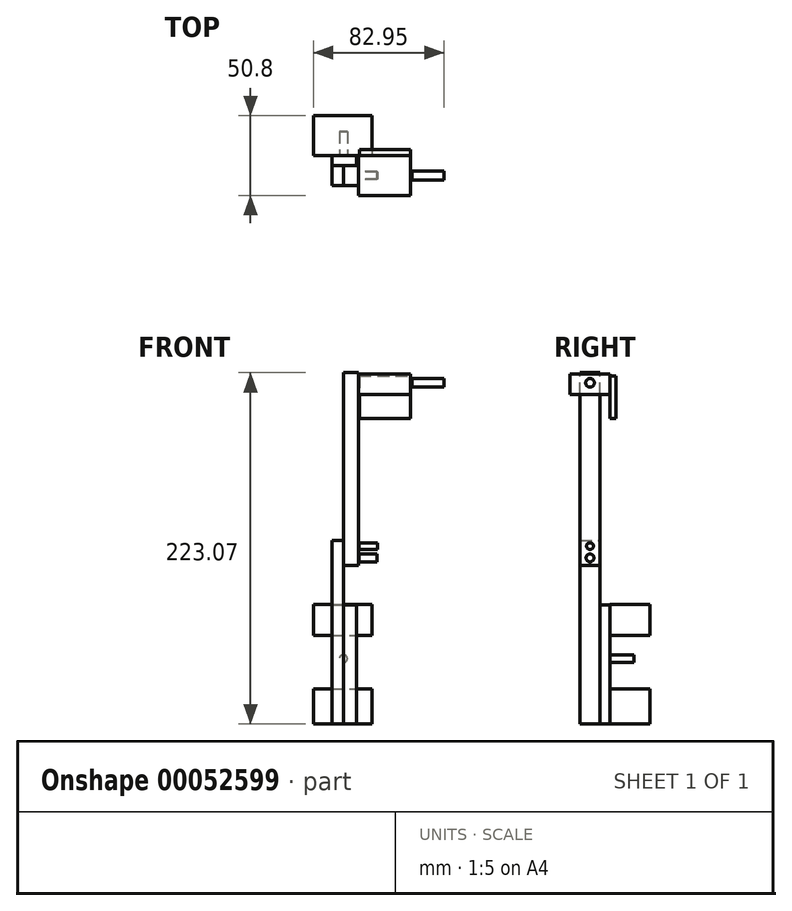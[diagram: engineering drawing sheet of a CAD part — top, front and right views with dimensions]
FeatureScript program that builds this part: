
annotation { "Feature Type Name" : "Feature", "Feature Type Description" : "" }
export const myFeature = defineFeature(function(context is Context, id is Id, definition is map)
    precondition{}
    {
        {
            var Q0;
            Q0=qCreatedBy(makeId("Front.planeOp"),FACE);
            var sketch = newSketch(context, id + "F0", { "sketchPlane" : qUnion([Q0])});
            skLineSegment(sketch, "E0.bottom", {"start": v(-19.02, 0) * mm, "end": v(18.3, 0) * mm});
            skLineSegment(sketch, "E0.top", {"start": v(-19.02, 22.12) * mm, "end": v(18.3, 22.12) * mm});
            skLineSegment(sketch, "E0.left", {"start": v(-19.02, 0) * mm, "end": v(-19.02, 22.12) * mm});
            skLineSegment(sketch, "E0.right", {"start": v(18.3, 0) * mm, "end": v(18.3, 22.12) * mm});
            skLineSegment(sketch, "E1.bottom", {"start": v(-19.02, 76) * mm, "end": v(18.3, 76) * mm});
            skLineSegment(sketch, "E1.top", {"start": v(-19.02, 56.34) * mm, "end": v(18.3, 56.34) * mm});
            skLineSegment(sketch, "E1.left", {"start": v(-19.02, 76) * mm, "end": v(-19.02, 56.34) * mm});
            skLineSegment(sketch, "E1.right", {"start": v(18.3, 76) * mm, "end": v(18.3, 56.34) * mm});
            skSolve(sketch);
        }
        {
            var Q0;
            Q0=qCreatedBy(makeId("Front.planeOp"),FACE);
            var sketch = newSketch(context, id + "F1", { "sketchPlane" : qUnion([Q0])});
            skLineSegment(sketch, "E2.bottom", {"start": v(-7.37, 75.64) * mm, "end": v(8.28, 75.64) * mm});
            skLineSegment(sketch, "E2.top", {"start": v(-7.37, 0) * mm, "end": v(8.28, 0) * mm});
            skLineSegment(sketch, "E2.left", {"start": v(-7.37, 75.64) * mm, "end": v(-7.37, 0) * mm});
            skLineSegment(sketch, "E2.right", {"start": v(8.28, 75.64) * mm, "end": v(8.28, 0) * mm});
            skSolve(sketch);
        }
        {
            var Q0;
            Q0 = qSketchRegion(id + "F0", true);
            extrude(context, id + "F2", {"entities" : qUnion([Q0]), "oppositeDirection" : true, "depth" : 25.4 * mm});
        }
        {
            var Q0;
            Q0 = qSketchRegion(id + "F1", true);
            extrude(context, id + "F3", {"entities" : qUnion([Q0]), "depth" : 6.35 * mm});
        }
        {
            var Q0;
            Q0=qCreatedBy(makeId("Front.planeOp"),FACE);
            var sketch = newSketch(context, id + "F4", { "sketchPlane" : qUnion([Q0])});
            skLineSegment(sketch, "E3.bottom", {"start": v(-7.32, 0) * mm, "end": v(0, 0) * mm});
            skLineSegment(sketch, "E3.top", {"start": v(-7.32, 116.65) * mm, "end": v(0, 116.65) * mm});
            skLineSegment(sketch, "E3.left", {"start": v(-7.32, 0) * mm, "end": v(-7.32, 116.65) * mm});
            skLineSegment(sketch, "E3.right", {"start": v(0, 0) * mm, "end": v(0, 116.65) * mm});
            skSolve(sketch);
        }
        {
            var Q0;
            Q0=qCreatedBy(makeId("Front.planeOp"),FACE);
            var sketch = newSketch(context, id + "F5", { "sketchPlane" : qUnion([Q0])});
            skLineSegment(sketch, "E4.bottom", {"start": v(0, 100.51) * mm, "end": v(9.56, 100.51) * mm});
            skLineSegment(sketch, "E4.top", {"start": v(0, 223.07) * mm, "end": v(9.56, 223.07) * mm});
            skLineSegment(sketch, "E4.left", {"start": v(0, 100.51) * mm, "end": v(0, 223.07) * mm});
            skLineSegment(sketch, "E4.right", {"start": v(9.56, 100.51) * mm, "end": v(9.56, 223.07) * mm});
            skSolve(sketch);
        }
        {
            var Q0;
            Q0=qCreatedBy(makeId("Front.planeOp"),FACE);
            var sketch = newSketch(context, id + "F6", { "sketchPlane" : qUnion([Q0])});
            skLineSegment(sketch, "E5.bottom", {"start": v(9.56, 222.15) * mm, "end": v(42.73, 222.15) * mm});
            skLineSegment(sketch, "E5.top", {"start": v(9.56, 209.25) * mm, "end": v(42.73, 209.25) * mm});
            skLineSegment(sketch, "E5.left", {"start": v(9.56, 222.15) * mm, "end": v(9.56, 209.25) * mm});
            skLineSegment(sketch, "E5.right", {"start": v(42.73, 222.15) * mm, "end": v(42.73, 209.25) * mm});
            skSolve(sketch);
        }
        {
            var Q0;
            Q0=qCreatedBy(makeId("Front.planeOp"),FACE);
            var sketch = newSketch(context, id + "F7", { "sketchPlane" : qUnion([Q0])});
            skLineSegment(sketch, "E6.bottom", {"start": v(43.66, 216.62) * mm, "end": v(63.93, 216.62) * mm});
            skLineSegment(sketch, "E6.top", {"start": v(43.66, 213.85) * mm, "end": v(63.93, 213.85) * mm});
            skLineSegment(sketch, "E6.left", {"start": v(43.66, 216.62) * mm, "end": v(43.66, 213.85) * mm});
            skLineSegment(sketch, "E6.right", {"start": v(63.93, 216.62) * mm, "end": v(63.93, 213.85) * mm});
            skSolve(sketch);
        }
        {
            var Q0;
            Q0=makeQuery(id+"F7.imprint","IMPRINT",FACE,{"disambiguationData":[TD([[makeQuery(id+"F7.imprint","IMPRINT",EDGE,{"derivedFrom":sQuery(id+"F7.wireOp",EDGE,"E6.bottom")}),-1.0]])]});
            var Q1;
            Q1=sQuery(id+"F7.wireOp",EDGE,"E6.bottom");
            revolve(context, id + "F8", {"entities" : qUnion([Q0]), "axis" : qUnion([Q1]), "revolveType" : RevolveType.FULL});
        }
        {
            var Q0;
            Q0=makeQuery(id+"F6.imprint","IMPRINT",FACE,{"disambiguationData":[TD([[makeQuery(id+"F6.imprint","IMPRINT",EDGE,{"derivedFrom":sQuery(id+"F6.wireOp",EDGE,"E5.bottom")}),-1.0]])]});
            extrude(context, id + "F9", {"entities" : qUnion([Q0]), "endBound" : BoundingType.SYMMETRIC, "depth" : 25.4 * mm});
        }
        {
            var Q0;
            Q0=makeQuery(id+"F4.imprint","IMPRINT",FACE,{"disambiguationData":[TD([[makeQuery(id+"F4.imprint","IMPRINT",EDGE,{"derivedFrom":sQuery(id+"F4.wireOp",EDGE,"E3.bottom")}),1.0]])]});
            extrude(context, id + "F10", {"entities" : qUnion([Q0]), "depth" : 12.7 * mm});
        }
        {
            var Q0;
            Q0=makeQuery(id+"F5.imprint","IMPRINT",FACE,{"disambiguationData":[TD([[makeQuery(id+"F5.imprint","IMPRINT",EDGE,{"derivedFrom":sQuery(id+"F5.wireOp",EDGE,"E4.bottom")}),1.0]])]});
            extrude(context, id + "F11", {"entities" : qUnion([Q0]), "depth" : 12.7 * mm});
        }
        {
            var Q0;
            Q0=qCreatedBy(makeId("Front.planeOp"),FACE);
            var sketch = newSketch(context, id + "F12", { "sketchPlane" : qUnion([Q0])});
            skLineSegment(sketch, "E7.bottom", {"start": v(9.83, 115.08) * mm, "end": v(21.63, 115.08) * mm});
            skLineSegment(sketch, "E7.top", {"start": v(9.83, 112.94) * mm, "end": v(21.63, 112.94) * mm});
            skLineSegment(sketch, "E7.left", {"start": v(9.83, 115.08) * mm, "end": v(9.83, 112.94) * mm});
            skLineSegment(sketch, "E7.right", {"start": v(21.63, 115.08) * mm, "end": v(21.63, 112.94) * mm});
            skSolve(sketch);
        }
        {
            var Q0;
            Q0=qCreatedBy(makeId("Front.planeOp"),FACE);
            var sketch = newSketch(context, id + "F13", { "sketchPlane" : qUnion([Q0])});
            skLineSegment(sketch, "E8.bottom", {"start": v(9.83, 102.93) * mm, "end": v(21.27, 102.93) * mm});
            skLineSegment(sketch, "E8.top", {"start": v(9.83, 105.43) * mm, "end": v(21.27, 105.43) * mm});
            skLineSegment(sketch, "E8.left", {"start": v(9.83, 102.93) * mm, "end": v(9.83, 105.43) * mm});
            skLineSegment(sketch, "E8.right", {"start": v(21.27, 102.93) * mm, "end": v(21.27, 105.43) * mm});
            skSolve(sketch);
        }
        {
            var Q0;
            Q0=makeQuery(id+"F12.imprint","IMPRINT",FACE,{"disambiguationData":[TD([[makeQuery(id+"F12.imprint","IMPRINT",EDGE,{"derivedFrom":sQuery(id+"F12.wireOp",EDGE,"E7.bottom")}),-1.0]])]});
            var Q1;
            Q1=sQuery(id+"F12.wireOp",EDGE,"E7.top");
            revolve(context, id + "F14", {"entities" : qUnion([Q0]), "axis" : qUnion([Q1]), "revolveType" : RevolveType.FULL});
        }
        {
            var Q0;
            Q0=makeQuery(id+"F13.imprint","IMPRINT",FACE,{"disambiguationData":[TD([[makeQuery(id+"F13.imprint","IMPRINT",EDGE,{"derivedFrom":sQuery(id+"F13.wireOp",EDGE,"E8.bottom")}),1.0]])]});
            var Q1;
            Q1=sQuery(id+"F13.wireOp",EDGE,"E8.top");
            revolve(context, id + "F15", {"entities" : qUnion([Q0]), "axis" : qUnion([Q1]), "revolveType" : RevolveType.FULL});
        }
        {
            var Q0;
            Q0=makeQuery(id+"F11.opExtrude","SWEPT_BODY",BODY,{"disambiguationData":[OSD([sQuery(id+"F5.wireOp",EDGE,"E4.bottom"),sQuery(id+"F5.wireOp",EDGE,"E4.top"),sQuery(id+"F5.wireOp",EDGE,"E4.left"),sQuery(id+"F5.wireOp",EDGE,"E4.right")])]});
            var Q1;
            Q1=makeQuery(id+"F10.opExtrude","SWEPT_BODY",BODY,{"disambiguationData":[OSD([sQuery(id+"F4.wireOp",EDGE,"E3.bottom"),sQuery(id+"F4.wireOp",EDGE,"E3.top"),sQuery(id+"F4.wireOp",EDGE,"E3.left"),sQuery(id+"F4.wireOp",EDGE,"E3.right")])]});
            var Q2;
            Q2=makeQuery(id+"F15.opRevolve","SWEPT_BODY",BODY,{"disambiguationData":[OSD([sQuery(id+"F13.wireOp",EDGE,"E8.bottom"),sQuery(id+"F13.wireOp",EDGE,"E8.top"),sQuery(id+"F13.wireOp",EDGE,"E8.left"),sQuery(id+"F13.wireOp",EDGE,"E8.right")])]});
            var Q3;
            Q3=makeQuery(id+"F14.opRevolve","SWEPT_BODY",BODY,{"disambiguationData":[OSD([sQuery(id+"F12.wireOp",EDGE,"E7.bottom"),sQuery(id+"F12.wireOp",EDGE,"E7.top"),sQuery(id+"F12.wireOp",EDGE,"E7.left"),sQuery(id+"F12.wireOp",EDGE,"E7.right")])]});
            var Q4;
            Q4=makeQuery(id+"F9.opExtrude","SWEPT_BODY",BODY,{"disambiguationData":[OSD([sQuery(id+"F6.wireOp",EDGE,"E5.bottom"),sQuery(id+"F6.wireOp",EDGE,"E5.top"),sQuery(id+"F6.wireOp",EDGE,"E5.left"),sQuery(id+"F6.wireOp",EDGE,"E5.right")])]});
            var Q5;
            Q5=makeQuery(id+"F8.opRevolve","SWEPT_BODY",BODY,{"disambiguationData":[OSD([sQuery(id+"F7.wireOp",EDGE,"E6.bottom"),sQuery(id+"F7.wireOp",EDGE,"E6.top"),sQuery(id+"F7.wireOp",EDGE,"E6.left"),sQuery(id+"F7.wireOp",EDGE,"E6.right")])]});
            var Q6;
            Q6=makeQuery(id+"F2.opExtrude","SWEPT_EDGE",EDGE,{"disambiguationData":[OSD([sQuery(id+"F0.wireOp",EDGE,"E0.bottom"),sQuery(id+"F0.wireOp",EDGE,"E0.left")])]});
            transform(context, id + "F16", {"entities" : qUnion([Q0, Q1, Q2, Q3, Q4, Q5]), "transformType" : TransformType.TRANSLATION_DISTANCE, "transformDirection" : qUnion([Q6]), "distance" : 6.35 * mm, "makeCopy" : false});
        }
        {
            var Q0;
            Q0=makeQuery(id+"F14.opRevolve","SWEPT_BODY",BODY,{"disambiguationData":[OSD([sQuery(id+"F12.wireOp",EDGE,"E7.bottom"),sQuery(id+"F12.wireOp",EDGE,"E7.top"),sQuery(id+"F12.wireOp",EDGE,"E7.left"),sQuery(id+"F12.wireOp",EDGE,"E7.right")])]});
            var Q1;
            Q1=makeQuery(id+"F15.opRevolve","SWEPT_BODY",BODY,{"disambiguationData":[OSD([sQuery(id+"F13.wireOp",EDGE,"E8.bottom"),sQuery(id+"F13.wireOp",EDGE,"E8.top"),sQuery(id+"F13.wireOp",EDGE,"E8.left"),sQuery(id+"F13.wireOp",EDGE,"E8.right")])]});
            var Q2;
            Q2=makeQuery(id+"F11.opExtrude","SWEPT_EDGE",EDGE,{"disambiguationData":[OSD([sQuery(id+"F5.wireOp",EDGE,"E4.bottom"),sQuery(id+"F5.wireOp",EDGE,"E4.right")])]});
            transform(context, id + "F17", {"entities" : qUnion([Q0, Q1]), "transformType" : TransformType.TRANSLATION_DISTANCE, "transformDirection" : qUnion([Q2]), "distance" : 6.35 * mm, "oppositeDirection" : true, "makeCopy" : false});
        }
        {
            var Q0;
            Q0=makeQuery(id+"F9.opExtrude","SWEPT_BODY",BODY,{"disambiguationData":[OSD([sQuery(id+"F6.wireOp",EDGE,"E5.bottom"),sQuery(id+"F6.wireOp",EDGE,"E5.top"),sQuery(id+"F6.wireOp",EDGE,"E5.left"),sQuery(id+"F6.wireOp",EDGE,"E5.right")])]});
            var Q1;
            Q1=makeQuery(id+"F8.opRevolve","SWEPT_BODY",BODY,{"disambiguationData":[OSD([sQuery(id+"F7.wireOp",EDGE,"E6.bottom"),sQuery(id+"F7.wireOp",EDGE,"E6.top"),sQuery(id+"F7.wireOp",EDGE,"E6.left"),sQuery(id+"F7.wireOp",EDGE,"E6.right")])]});
            var Q2;
            Q2=makeQuery(id+"F11.opExtrude","SWEPT_EDGE",EDGE,{"disambiguationData":[OSD([sQuery(id+"F5.wireOp",EDGE,"E4.top"),sQuery(id+"F5.wireOp",EDGE,"E4.right")])]});
            transform(context, id + "F18", {"entities" : qUnion([Q0, Q1]), "transformType" : TransformType.TRANSLATION_DISTANCE, "transformDirection" : qUnion([Q2]), "distance" : 6.35 * mm, "oppositeDirection" : true, "makeCopy" : false});
        }
        {
            var Q0;
            Q0=qCreatedBy(makeId("Front.planeOp"),FACE);
            var sketch = newSketch(context, id + "F19", { "sketchPlane" : qUnion([Q0])});
            skLineSegment(sketch, "E9.bottom", {"start": v(10.19, 220.9) * mm, "end": v(42.72, 220.9) * mm});
            skLineSegment(sketch, "E9.top", {"start": v(10.19, 194.09) * mm, "end": v(42.72, 194.09) * mm});
            skLineSegment(sketch, "E9.left", {"start": v(10.19, 220.9) * mm, "end": v(10.19, 194.09) * mm});
            skLineSegment(sketch, "E9.right", {"start": v(42.72, 220.9) * mm, "end": v(42.72, 194.09) * mm});
            skSolve(sketch);
        }
        {
            var Q0;
            Q0=makeQuery(id+"F19.imprint","IMPRINT",FACE,{"disambiguationData":[TD([[makeQuery(id+"F19.imprint","IMPRINT",EDGE,{"derivedFrom":sQuery(id+"F19.wireOp",EDGE,"E9.bottom")}),-1.0]])]});
            extrude(context, id + "F20", {"entities" : qUnion([Q0]), "operationType" : NewBodyOperationType.ADD, "oppositeDirection" : true, "depth" : 3.8 * mm});
        }
        {
            var Q0;
            Q0=qCreatedBy(makeId("Right.planeOp"),FACE);
            var sketch = newSketch(context, id + "F21", { "sketchPlane" : qUnion([Q0])});
            skLineSegment(sketch, "E10.bottom", {"start": v(0, 43.94) * mm, "end": v(15.2, 43.94) * mm});
            skLineSegment(sketch, "E10.top", {"start": v(0, 41.44) * mm, "end": v(15.2, 41.44) * mm});
            skLineSegment(sketch, "E10.left", {"start": v(0, 43.94) * mm, "end": v(0, 41.44) * mm});
            skLineSegment(sketch, "E10.right", {"start": v(15.2, 43.94) * mm, "end": v(15.2, 41.44) * mm});
            skSolve(sketch);
        }
        {
            var Q0;
            Q0=makeQuery(id+"F21.imprint","IMPRINT",FACE,{"disambiguationData":[TD([[makeQuery(id+"F21.imprint","IMPRINT",EDGE,{"derivedFrom":sQuery(id+"F21.wireOp",EDGE,"E10.bottom")}),-1.0]])]});
            var Q1;
            Q1=sQuery(id+"F21.wireOp",EDGE,"E10.top");
            revolve(context, id + "F22", {"operationType" : NewBodyOperationType.ADD, "entities" : qUnion([Q0]), "axis" : qUnion([Q1]), "revolveType" : RevolveType.FULL});
        }
    });
